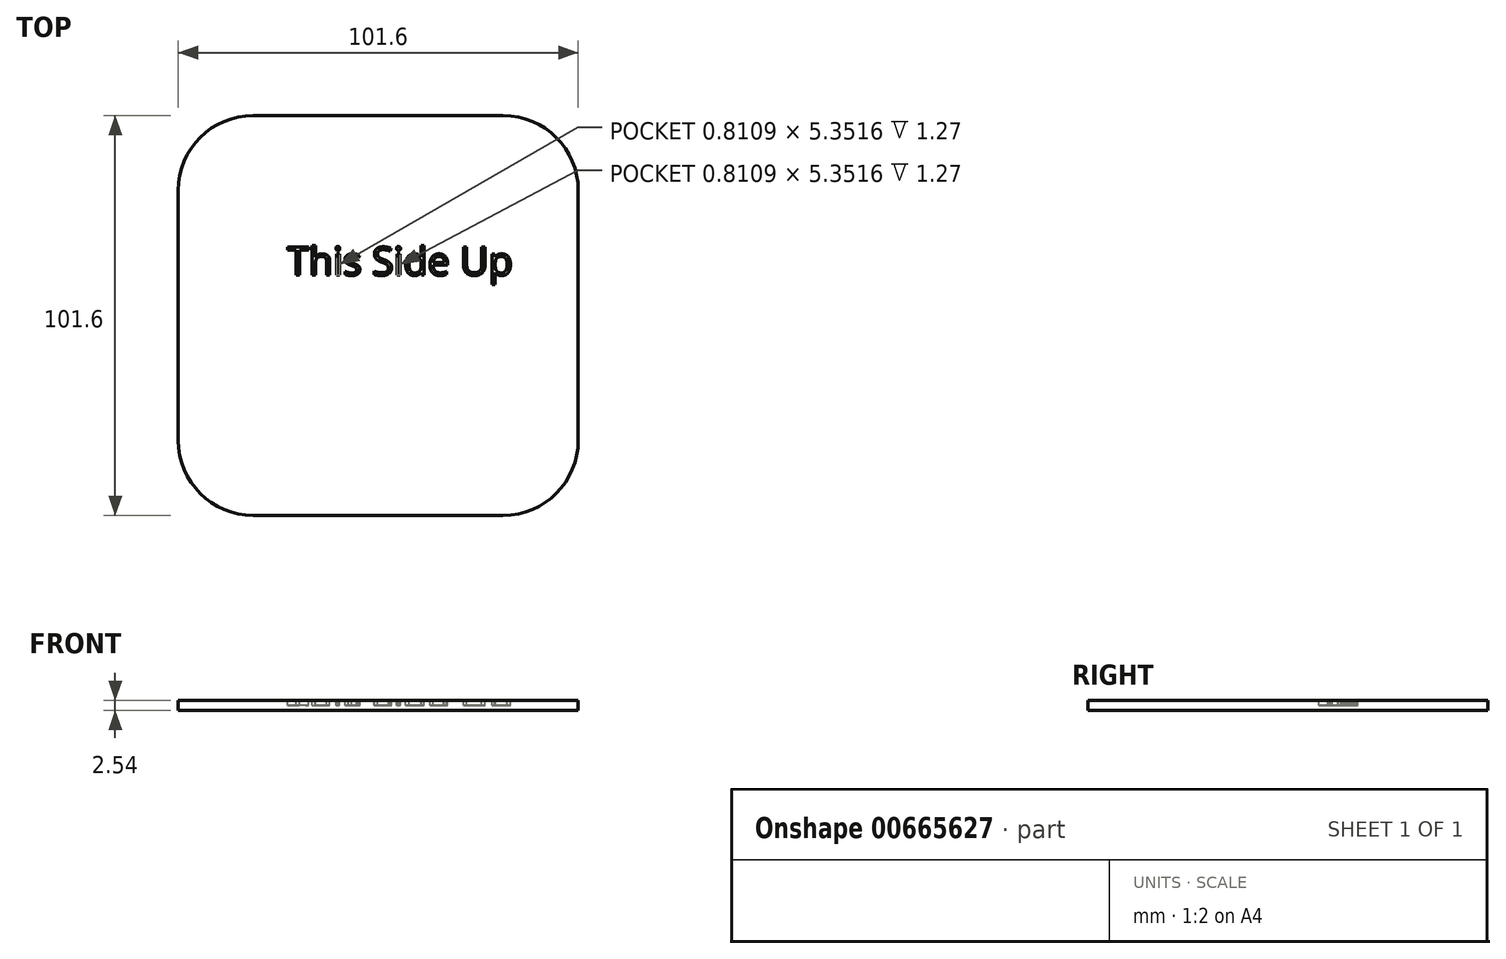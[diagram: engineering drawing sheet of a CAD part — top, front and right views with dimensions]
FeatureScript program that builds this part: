
annotation { "Feature Type Name" : "Feature", "Feature Type Description" : "" }
export const myFeature = defineFeature(function(context is Context, id is Id, definition is map)
    precondition{}
    {
        {
            var Q0;
            Q0=qCreatedBy(makeId("Top.planeOp"),FACE);
            var sketch = newSketch(context, id + "F0", { "sketchPlane" : qUnion([Q0])});
            skLineSegment(sketch, "E0.bottom", {"start": v(31.75, 50.8) * mm, "end": v(-31.75, 50.8) * mm});
            skLineSegment(sketch, "E0.top", {"start": v(31.75, -50.8) * mm, "end": v(-31.75, -50.8) * mm});
            skLineSegment(sketch, "E0.left", {"start": v(50.8, 31.75) * mm, "end": v(50.8, -31.75) * mm});
            skLineSegment(sketch, "E0.right", {"start": v(-50.8, 31.75) * mm, "end": v(-50.8, -31.75) * mm});
            skPoint(sketch, "E0.middle", {"position": v(0, 0) * mm});
            skPoint(sketch, "E1.visualSharp", {"position": v(-50.8, 50.8) * mm});
            skArc(sketch, "E1.filletArc", {"start": v(-31.75, 50.8) * mm, "mid": v(-45.22, 45.22) * mm, "end": v(-50.8, 31.75) * mm});
            skPoint(sketch, "E2.visualSharp", {"position": v(50.8, 50.8) * mm});
            skArc(sketch, "E2.filletArc", {"start": v(50.8, 31.75) * mm, "mid": v(45.22, 45.22) * mm, "end": v(31.75, 50.8) * mm});
            skPoint(sketch, "E3.visualSharp", {"position": v(50.8, -50.8) * mm});
            skArc(sketch, "E3.filletArc", {"start": v(31.75, -50.8) * mm, "mid": v(45.22, -45.22) * mm, "end": v(50.8, -31.75) * mm});
            skPoint(sketch, "E4.visualSharp", {"position": v(-50.8, -50.8) * mm});
            skArc(sketch, "E4.filletArc", {"start": v(-50.8, -31.75) * mm, "mid": v(-45.22, -45.22) * mm, "end": v(-31.75, -50.8) * mm});
            skSolve(sketch);
        }
        {
            var Q0;
            Q0 = qSketchRegion(id + "F0", true);
            extrude(context, id + "F1", {"entities" : qUnion([Q0]), "depth" : 2.54 * mm, "offsetDistance" : 25.4 * mm});
        }
        {
            var Q0;
            Q0=makeQuery(id+"F1.opExtrude","CAP_FACE",FACE,{"disambiguationData":[OSD([sQuery(id+"F0.wireOp",EDGE,"E0.bottom"),sQuery(id+"F0.wireOp",EDGE,"E0.top"),sQuery(id+"F0.wireOp",EDGE,"E0.left"),sQuery(id+"F0.wireOp",EDGE,"E0.right"),sQuery(id+"F0.wireOp",EDGE,"E1.filletArc"),sQuery(id+"F0.wireOp",EDGE,"E2.filletArc"),sQuery(id+"F0.wireOp",EDGE,"E3.filletArc"),sQuery(id+"F0.wireOp",EDGE,"E4.filletArc")])],"isStart":false});
            var sketch = newSketch(context, id + "F2", { "sketchPlane" : qUnion([Q0])});
            skText(sketch, "E5", { "text": "This Side Up", "fontName": "OpenSans-Regular.ttf"});
            const initialGuessF2  = {"E5": [-0.02317, 0.01022, 1, 0, 0.0072]};
            skSetInitialGuess(sketch, initialGuessF2);
            skSolve(sketch);
        }
        {
            var Q0;
            Q0 = qSketchRegion(id + "F2", true);
            extrude(context, id + "F3", {"entities" : qUnion([Q0]), "operationType" : NewBodyOperationType.REMOVE, "oppositeDirection" : true, "depth" : 1.27 * mm, "offsetDistance" : 25.4 * mm});
        }
    });
